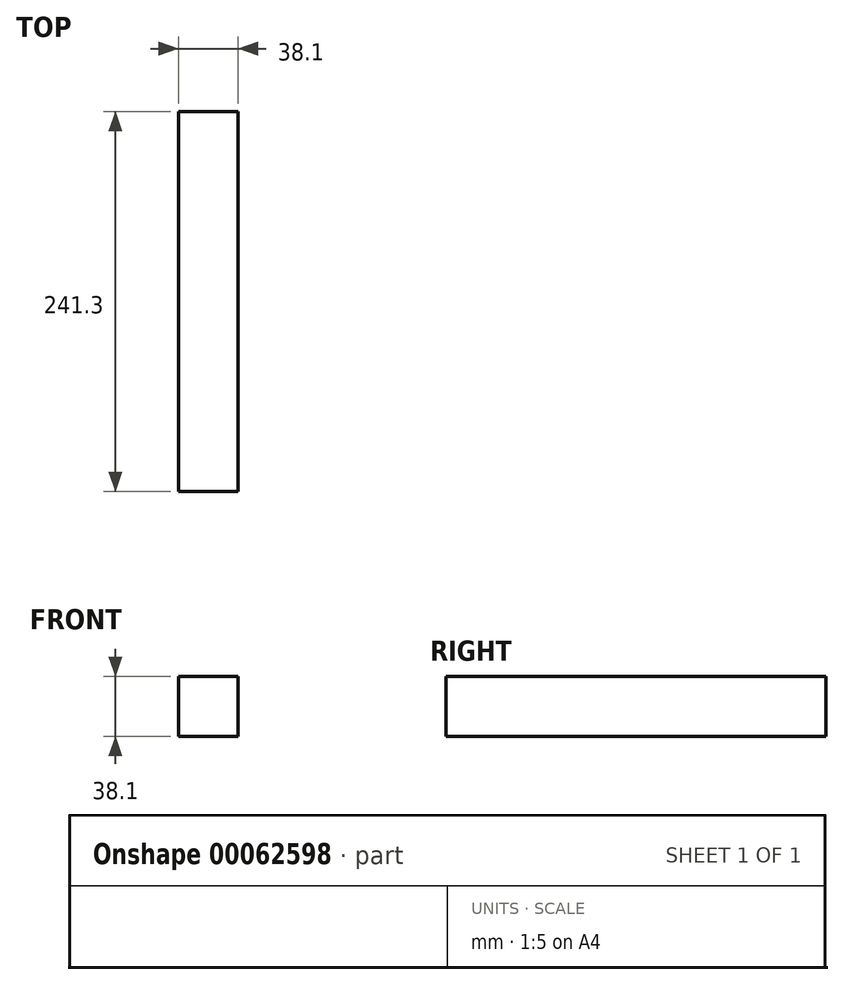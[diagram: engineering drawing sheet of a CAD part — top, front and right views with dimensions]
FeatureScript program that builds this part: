
annotation { "Feature Type Name" : "Feature", "Feature Type Description" : "" }
export const myFeature = defineFeature(function(context is Context, id is Id, definition is map)
    precondition{}
    {
        {
            var Q0;
            Q0=qCreatedBy(makeId("Front.planeOp"),FACE);
            var sketch = newSketch(context, id + "F0", { "sketchPlane" : qUnion([Q0])});
            skLineSegment(sketch, "E0.bottom", {"start": v(0, 0) * mm, "end": v(38.1, 0) * mm});
            skLineSegment(sketch, "E0.top", {"start": v(0, 38.1) * mm, "end": v(38.1, 38.1) * mm});
            skLineSegment(sketch, "E0.left", {"start": v(0, 0) * mm, "end": v(0, 38.1) * mm});
            skLineSegment(sketch, "E0.right", {"start": v(38.1, 0) * mm, "end": v(38.1, 38.1) * mm});
            skSolve(sketch);
        }
        {
            var Q0;
            Q0=makeQuery(id+"F0.imprint","IMPRINT",FACE,{"disambiguationData":[TD([[makeQuery(id+"F0.imprint","IMPRINT",EDGE,{"derivedFrom":sQuery(id+"F0.wireOp",EDGE,"E0.bottom")}),1.0]])]});
            extrude(context, id + "F1", {"entities" : qUnion([Q0]), "depth" : 241.3 * mm});
        }
    });
